# Revit family: LHFL-Recessed Troffer
name_source: partatom
category: Lighting Fixtures
units: mm (PartAtom-declared; Revit-internal decimal feet)

## family parameters
Cut with Voids When Loaded = No
Host = Face
Light Source = Yes
OmniClass Number = 23.80.70.11.14.17
OmniClass Title = Direct/Indirect
Part Type = Normal
Room Calculation Point = No
Round Connector Dimension = Use Diameter
Shared = Yes

## types (3) — shared parameters
Apparent Load = 0 VA
Assembly Code = D5020210
Backbox = Paint -  Matte White
Color Filter = 16777215
Default Elevation = 48 "
Description = Litewave™ LHF Recessed Troffer
Diffuser = Soft Glow Lens, Blade Baffle, Perforated Blade
Dimming Lamp Color Temperature Shift = <None>
Distribution = Direct
Emit Shape Visible in Rendering = No
Glass = Glass - White
Lamp = Fluorescent
Load Classification = Lighting
Manufacturer = Litecontrol
Model = LHF
Mounting = Grid Ceiling, Narrow Face, Screw Slot
Photometric Web File = generic
Power Factor = 1
Tilt Angle = -90.00°
Type Comments = Lighting Fixtures
URL = https://www.currentlighting.com
Voltage = 120 V
Warranty = 1 year warranty

## per-type parameters (varying)
| type | Emit from Rectangle Length | Emit from Rectangle Width | zz Length 1 | zz Length 2 |
| LHF-2x2 | 23 " | 23 " | 24 " | 24 " |
| LHF-2x4 | 47 " | 23 " | 48 " | 24 " |
| LHF-1x4 | 47 " | 11 " | 48 " | 12 " |

## geometry (parser evidence)
native form markers: Sweep x6
no freeform markers — native parametric forms only
